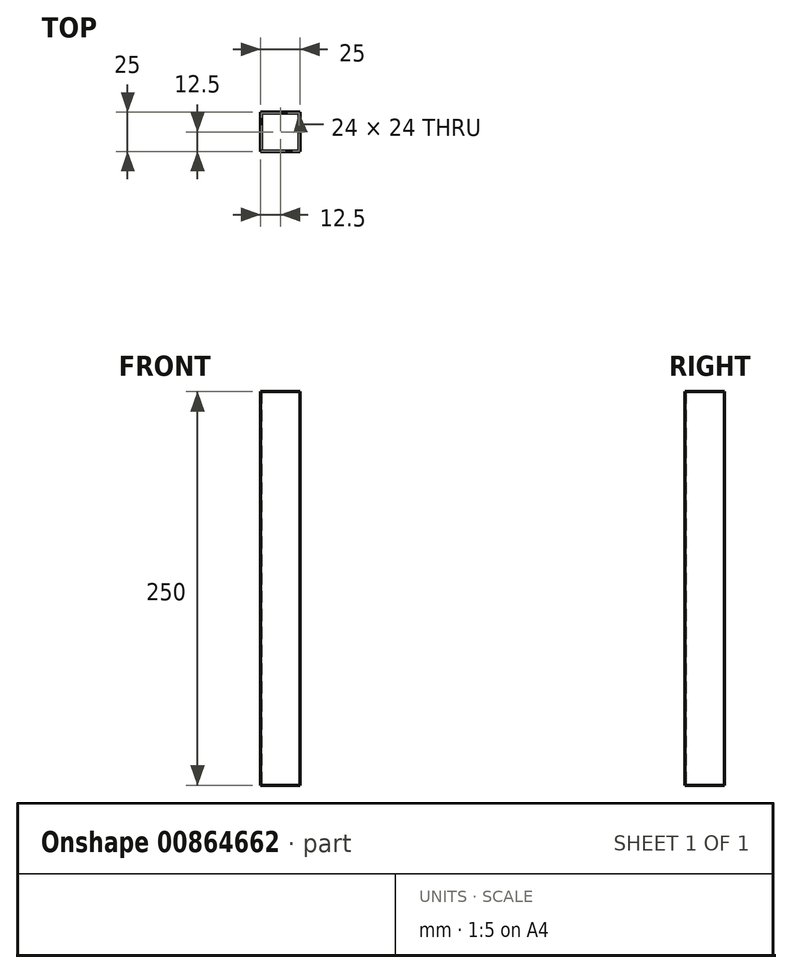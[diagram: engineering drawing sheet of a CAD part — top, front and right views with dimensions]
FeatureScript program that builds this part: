
annotation { "Feature Type Name" : "Feature", "Feature Type Description" : "" }
export const myFeature = defineFeature(function(context is Context, id is Id, definition is map)
    precondition{}
    {
        {
            var Q0;
            Q0=qCreatedBy(makeId("Top.planeOp"),FACE);
            var sketch = newSketch(context, id + "F0", { "sketchPlane" : qUnion([Q0])});
            skLineSegment(sketch, "E0.bottom", {"start": v(0, 0) * mm, "end": v(25, 0) * mm});
            skLineSegment(sketch, "E0.top", {"start": v(0, -25) * mm, "end": v(25, -25) * mm});
            skLineSegment(sketch, "E0.left", {"start": v(0, 0) * mm, "end": v(0, -25) * mm});
            skLineSegment(sketch, "E0.right", {"start": v(25, 0) * mm, "end": v(25, -25) * mm});
            skLineSegment(sketch, "E1.bottom", {"start": v(0.5, -0.5) * mm, "end": v(24.5, -0.5) * mm});
            skLineSegment(sketch, "E1.top", {"start": v(0.5, -24.5) * mm, "end": v(24.5, -24.5) * mm});
            skLineSegment(sketch, "E1.left", {"start": v(0.5, -0.5) * mm, "end": v(0.5, -24.5) * mm});
            skLineSegment(sketch, "E1.right", {"start": v(24.5, -0.5) * mm, "end": v(24.5, -24.5) * mm});
            skSolve(sketch);
        }
        {
            var Q0;
            Q0 = qSketchRegion(id + "F0", true);
            extrude(context, id + "F1", {"entities" : qUnion([Q0]), "depth" : 250 * mm, "offsetDistance" : 25 * mm});
        }
    });
